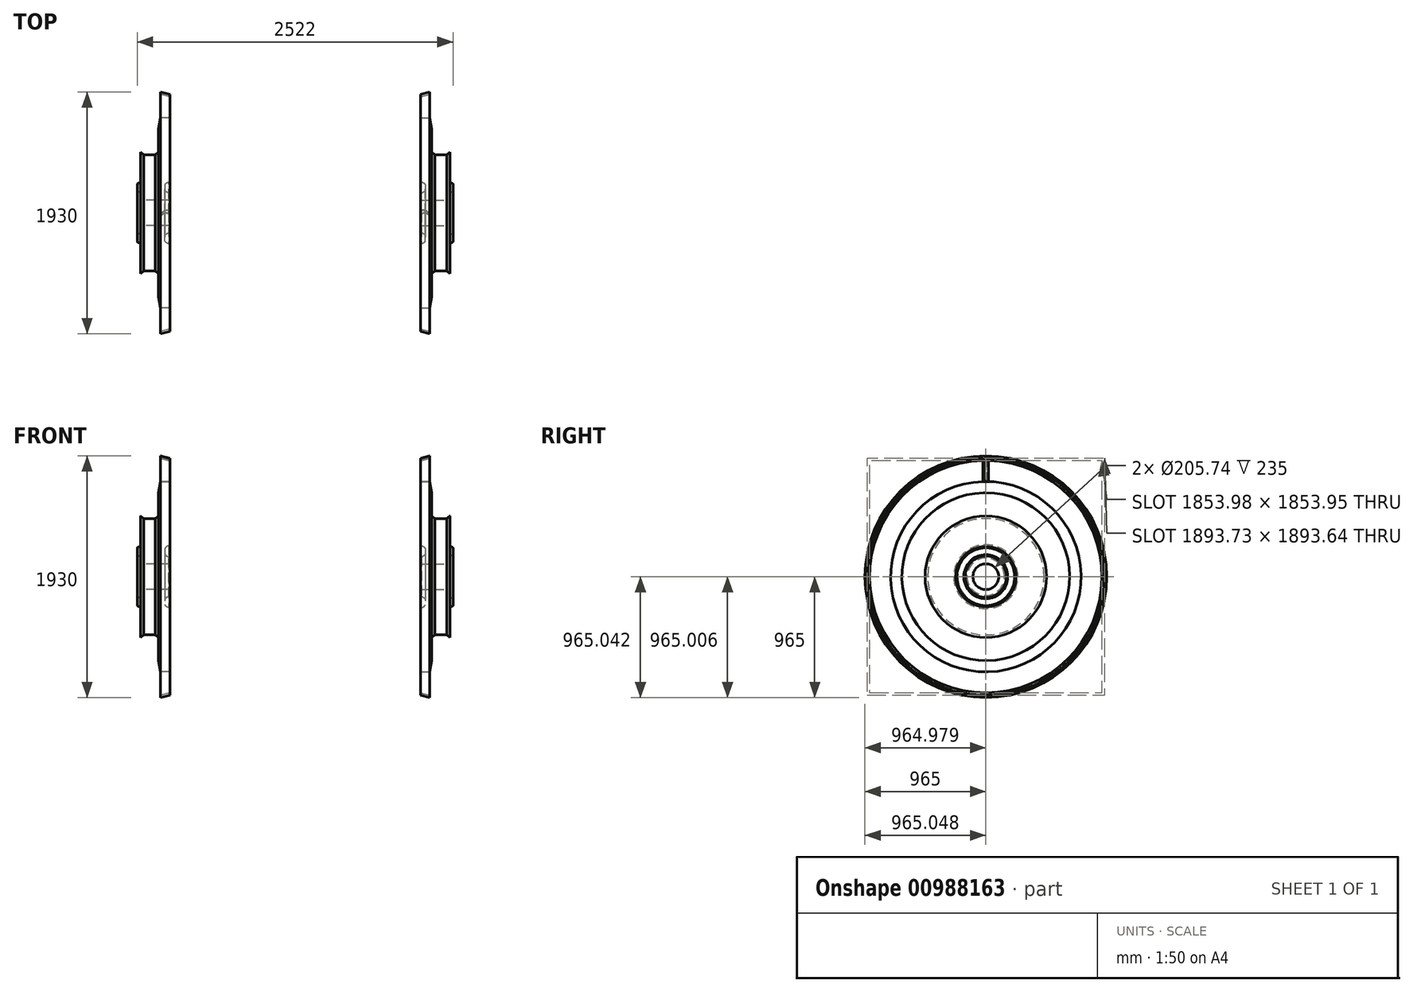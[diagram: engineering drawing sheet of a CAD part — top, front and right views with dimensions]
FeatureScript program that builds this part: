
annotation { "Feature Type Name" : "Feature", "Feature Type Description" : "" }
export const myFeature = defineFeature(function(context is Context, id is Id, definition is map)
    precondition{}
    {
        {
            var Q0;
            Q0=qCreatedBy(makeId("Top.planeOp"),FACE);
            var sketch = newSketch(context, id + "F0", { "sketchPlane" : qUnion([Q0])});
            skLineSegment(sketch, "E0", {"start": v(-458.73, 0) * mm, "end": v(0, 0) * mm, "construction": true});
            skLineSegment(sketch, "E1", {"start": v(0, 760) * mm, "end": v(-75, 760) * mm});
            skLineSegment(sketch, "E2", {"start": v(-115, 465) * mm, "end": v(-210, 465) * mm});
            skLineSegment(sketch, "E3", {"start": v(-210, 465) * mm, "end": v(-235, 485) * mm});
            skLineSegment(sketch, "E4", {"start": v(-235, 485) * mm, "end": v(-235, 240.87) * mm});
            skLineSegment(sketch, "E5", {"start": v(-235, 102.87) * mm, "end": v(0, 102.87) * mm});
            skLineSegment(sketch, "E6", {"start": v(0, 102.87) * mm, "end": v(0, 157.87) * mm});
            skLineSegment(sketch, "E7", {"start": v(-75, 965) * mm, "end": v(-75, 947) * mm});
            skLineSegment(sketch, "E8", {"start": v(-75, 947) * mm, "end": v(0, 927) * mm});
            skLineSegment(sketch, "E9", {"start": v(0, 927) * mm, "end": v(0, 945) * mm});
            skLineSegment(sketch, "E10", {"start": v(0, 945) * mm, "end": v(-75, 965) * mm});
            skLineSegment(sketch, "E11", {"start": v(-75, 760) * mm, "end": v(-75, 947) * mm, "construction": true});
            skLineSegment(sketch, "E12", {"start": v(-90, 485) * mm, "end": v(-90, 670) * mm});
            skLineSegment(sketch, "E13", {"start": v(-90, 670) * mm, "end": v(-75, 760) * mm});
            skLineSegment(sketch, "E14", {"start": v(-90, 485) * mm, "end": v(-115, 465) * mm});
            skLineSegment(sketch, "E15", {"start": v(-90, 485) * mm, "end": v(-235, 485) * mm, "construction": true});
            skArc(sketch, "E16", {"start": v(-235, 164.87) * mm, "mid": v(-248.98, 167.54) * mm, "end": v(-261, 175.16) * mm});
            skLineSegment(sketch, "E17", {"start": v(-261, 230.58) * mm, "end": v(-261, 175.16) * mm});
            skArc(sketch, "E18.trimOffspring", {"start": v(-261, 230.58) * mm, "mid": v(-248.98, 238.2) * mm, "end": v(-235, 240.87) * mm});
            skLineSegment(sketch, "E19.trimOffspring", {"start": v(-235, 164.87) * mm, "end": v(-235, 102.87) * mm});
            skArc(sketch, "E20", {"start": v(-235, 164.87) * mm, "mid": v(-273, 202.87) * mm, "end": v(-235, 240.87) * mm, "construction": true});
            skLineSegment(sketch, "E21", {"start": v(-235, 202.87) * mm, "end": v(0, 202.87) * mm, "construction": true});
            skArc(sketch, "E22", {"start": v(0, 157.87) * mm, "mid": v(-22.53, 163.91) * mm, "end": v(-39, 180.42) * mm});
            skLineSegment(sketch, "E23", {"start": v(-39, 225.32) * mm, "end": v(-39, 180.42) * mm});
            skArc(sketch, "E24.trimOffspring", {"start": v(-39, 225.32) * mm, "mid": v(-22.53, 241.83) * mm, "end": v(0, 247.87) * mm});
            skLineSegment(sketch, "E25.trimOffspring", {"start": v(0, 247.87) * mm, "end": v(0, 760) * mm});
            skArc(sketch, "E26", {"start": v(0, 157.87) * mm, "mid": v(-45, 202.87) * mm, "end": v(0, 247.87) * mm, "construction": true});
            skSolve(sketch);
        }
        {
            var Q0;
            Q0=makeQuery(id+"F0.imprint","IMPRINT",FACE,{"disambiguationData":[TD([[makeQuery(id+"F0.imprint","IMPRINT",EDGE,{"derivedFrom":sQuery(id+"F0.wireOp",EDGE,"E7")}),1.0]])]});
            var Q1;
            Q1=makeQuery(id+"F0.imprint","IMPRINT",FACE,{"disambiguationData":[TD([[makeQuery(id+"F0.imprint","IMPRINT",EDGE,{"derivedFrom":sQuery(id+"F0.wireOp",EDGE,"E1")}),1.0]])]});
            var Q2;
            Q2=sQuery(id+"F0.wireOp",EDGE,"E0");
            revolve(context, id + "F1", {"surfaceOperationType" : NewSurfaceOperationType.NEW, "entities" : qUnion([Q0, Q1]), "axis" : qUnion([Q2]), "revolveType" : RevolveType.FULL});
        }
        {
            var Q0;
            Q0=makeQuery(id+"F1.opRevolve","SWEPT_EDGE",EDGE,{"disambiguationData":[OSD([sQuery(id+"F0.wireOp",EDGE,"E24.trimOffspring"),sQuery(id+"F0.wireOp",EDGE,"E25.trimOffspring")])]});
            var Q1;
            Q1=makeQuery(id+"F1.opRevolve","SWEPT_EDGE",EDGE,{"disambiguationData":[OSD([sQuery(id+"F0.wireOp",EDGE,"E6"),sQuery(id+"F0.wireOp",EDGE,"E22")])]});
            chamfer(context, id + "F2", {"entities" : qUnion([Q0, Q1]), "width" : 9 * mm, "tangentPropagation" : true});
        }
        {
            var Q0;
            Q0=qCreatedBy(makeId("Right.planeOp"),FACE);
            var sketch = newSketch(context, id + "F3", { "sketchPlane" : qUnion([Q0])});
            skLineSegment(sketch, "E27", {"start": v(0, 0) * mm, "end": v(0, 760) * mm, "construction": true});
            skLineSegment(sketch, "E28", {"start": v(0, 0) * mm, "end": v(0, 945) * mm, "construction": true});
            skCircle(sketch, "E29.0", {"center": v(0, 0) * mm, "radius": 945 * mm, "construction": true});
            skCircle(sketch, "E30.0", {"center": v(0, 0) * mm, "radius": 760 * mm, "construction": true});
            skSolve(sketch);
        }
        {
            var Q0;
            Q0=qCreatedBy(makeId("Front.planeOp"),FACE);
            var sketch = newSketch(context, id + "F4", { "sketchPlane" : qUnion([Q0])});
            skLineSegment(sketch, "E31", {"start": v(-75, 965) * mm, "end": v(0, 945) * mm, "construction": true});
            skLineSegment(sketch, "E32", {"start": v(-37.5, 955) * mm, "end": v(-50.38, 906.69) * mm, "construction": true});
            skSolve(sketch);
        }
        {
            var Q0;
            Q0=sQuery(id+"F4.wireOp",EDGE,"E31");
            cPoint(context, id + "F5", {"entities" : qUnion([Q0]), "parameter" : 0.5});
        }
        {
            var Q0;
            Q0 = qCreatedBy(id + "F5" ,VERTEX);
            var Q1;
            Q1=sQuery(id+"F4.wireOp",EDGE,"E32");
            cPlane(context, id + "F6", {"entities" : qUnion([Q0, Q1]), "cplaneType" : CPlaneType.LINE_POINT, "offset" : 25 * mm, "width" : 150 * mm, "height" : 150 * mm});
        }
        {
            var Q0;
            Q0=sQuery(id+"F3.wireOp",VERTEX,"E27.end");
            var Q1;
            Q1=sQuery(id+"F3.wireOp",EDGE,"E28");
            cPlane(context, id + "F7", {"entities" : qUnion([Q0, Q1]), "cplaneType" : CPlaneType.LINE_POINT, "offset" : 25 * mm, "width" : 150 * mm, "height" : 150 * mm});
        }
        {
            var Q0;
            Q0=qCreatedBy(id+"F7.planeOp",FACE);
            cPlane(context, id + "F8", {"entities" : qUnion([Q0]), "cplaneType" : CPlaneType.OFFSET, "offset" : 1 * mm, "oppositeDirection" : true, "width" : 150 * mm, "height" : 150 * mm});
        }
        {
            var Q0;
            Q0=qCreatedBy(id+"F6.planeOp",FACE);
            cPlane(context, id + "F9", {"entities" : qUnion([Q0]), "cplaneType" : CPlaneType.OFFSET, "offset" : 5 * mm, "width" : 150 * mm, "height" : 150 * mm});
        }
        {
            var Q0;
            Q0=qCreatedBy(id+"F8.planeOp",FACE);
            var sketch = newSketch(context, id + "F10", { "sketchPlane" : qUnion([Q0])});
            skLineSegment(sketch, "E33.0", {"start": v(-75, -760) * mm, "end": v(-75, 760) * mm, "construction": true});
            skLineSegment(sketch, "E34.0", {"start": v(0, 760) * mm, "end": v(0, -760) * mm, "construction": true});
            skLineSegment(sketch, "E35", {"start": v(0, 0) * mm, "end": v(0, 15) * mm});
            skLineSegment(sketch, "E36", {"start": v(-75, -11.9) * mm, "end": v(-75, -21.9) * mm});
            skFitSpline(sketch, "E37", {"points": [v(0, 15) * mm, v(-27.98, 21.95) * mm, v(-48.46, 15) * mm, v(-75, -11.9) * mm], "startDerivative": vector(-101.16, 69.07) * mm, "endDerivative": vector(-58.12, -78.29) * mm});
            skFitSpline(sketch, "E38", {"points": [v(0, 0) * mm, v(-12.16, -4.34) * mm, v(-32.08, 1.17) * mm, v(-75, -21.9) * mm], "startDerivative": vector(-36.35, -51.97) * mm, "endDerivative": vector(-94.6, -79.28) * mm});
            skSolve(sketch);
        }
        {
            var Q0;
            Q0=qCreatedBy(id+"F9.planeOp",FACE);
            var sketch = newSketch(context, id + "F11", { "sketchPlane" : qUnion([Q0])});
            skLineSegment(sketch, "E39", {"start": v(-319.78, 23.36) * mm, "end": v(-319.78, 13.36) * mm});
            skFitSpline(sketch, "E40", {"points": [v(-242.16, 2.4) * mm, v(-256.13, 5.72) * mm, v(-275.43, 0) * mm, v(-319.78, 23.36) * mm], "startDerivative": vector(-83.26, 57.64) * mm, "endDerivative": vector(-92.17, 69.89) * mm});
            skFitSpline(sketch, "E41", {"points": [v(-242.16, -12.6) * mm, v(-270.9, -20.4) * mm, v(-291.95, -13.02) * mm, v(-319.78, 13.36) * mm], "startDerivative": vector(-80.99, -68.84) * mm, "endDerivative": vector(-67.6, 81.83) * mm});
            skLineSegment(sketch, "E42", {"start": v(-319.78, -99.8) * mm, "end": v(-319.78, 99.8) * mm, "construction": true});
            skLineSegment(sketch, "E43", {"start": v(-242.16, 98.76) * mm, "end": v(-242.16, -98.76) * mm, "construction": true});
            skLineSegment(sketch, "E44", {"start": v(-242.16, -12.6) * mm, "end": v(-242.16, 2.4) * mm});
            skSolve(sketch);
        }
        {
            var Q2;
            Q2=qSketchRegion(id+"F10",true);
            var Q3;
            Q3=qSketchRegion(id+"F11",true);
            loft(context, id + "F12", {"operationType" : NewBodyOperationType.ADD, "sheetProfilesArray" : [{ "sheetProfileEntities" : qUnion([Q2]) }, { "sheetProfileEntities" : qUnion([Q3]) }]});
        }
        {
            var Q0;
            Q0=qCreatedBy(makeId("Right.planeOp"),FACE);
            cPlane(context, id + "F13", {"entities" : qUnion([Q0]), "cplaneType" : CPlaneType.OFFSET, "offset" : 1000 * mm, "width" : 150 * mm, "height" : 150 * mm});
        }
        {
            var Q0;
            Q0=makeQuery(id+"F1.opRevolve","SWEPT_BODY",BODY,{"disambiguationData":[OSD([sQuery(id+"F0.wireOp",EDGE,"E1"),sQuery(id+"F0.wireOp",EDGE,"E2"),sQuery(id+"F0.wireOp",EDGE,"E3"),sQuery(id+"F0.wireOp",EDGE,"E4"),sQuery(id+"F0.wireOp",EDGE,"E5"),sQuery(id+"F0.wireOp",EDGE,"E6"),sQuery(id+"F0.wireOp",EDGE,"E12"),sQuery(id+"F0.wireOp",EDGE,"E13"),sQuery(id+"F0.wireOp",EDGE,"E14"),sQuery(id+"F0.wireOp",EDGE,"E16"),sQuery(id+"F0.wireOp",EDGE,"E17"),sQuery(id+"F0.wireOp",EDGE,"E18.trimOffspring"),sQuery(id+"F0.wireOp",EDGE,"E19.trimOffspring"),sQuery(id+"F0.wireOp",EDGE,"E22"),sQuery(id+"F0.wireOp",EDGE,"E23"),sQuery(id+"F0.wireOp",EDGE,"E24.trimOffspring"),sQuery(id+"F0.wireOp",EDGE,"E25.trimOffspring")])]});
            var Q1;
            Q1=qCreatedBy(id+"F13.planeOp",FACE);
            mirror(context, id + "F14", {"entities" : qUnion([Q0]), "mirrorPlane" : qUnion([Q1])});
        }
    });
